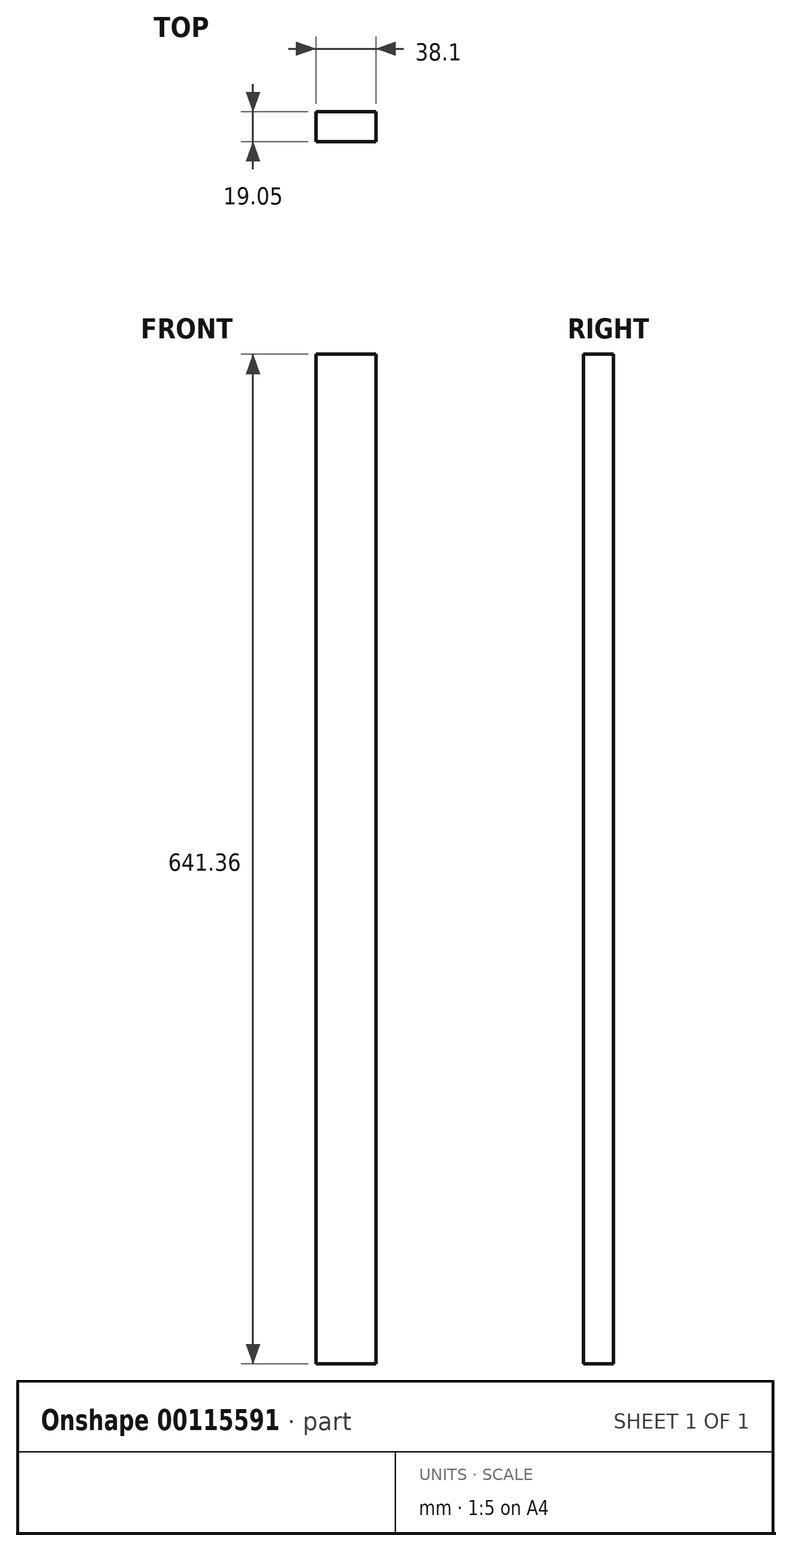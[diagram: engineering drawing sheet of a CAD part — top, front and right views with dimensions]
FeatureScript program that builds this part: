
annotation { "Feature Type Name" : "Feature", "Feature Type Description" : "" }
export const myFeature = defineFeature(function(context is Context, id is Id, definition is map)
    precondition{}
    {
        {
            var Q0;
            Q0=qCreatedBy(makeId("Front.planeOp"),FACE);
            var sketch = newSketch(context, id + "F0", { "sketchPlane" : qUnion([Q0])});
            skLineSegment(sketch, "E0.bottom", {"start": v(-19.05, 320.68) * mm, "end": v(19.05, 320.68) * mm});
            skLineSegment(sketch, "E0.top", {"start": v(-19.05, -320.68) * mm, "end": v(19.05, -320.68) * mm});
            skLineSegment(sketch, "E0.left", {"start": v(-19.05, 320.68) * mm, "end": v(-19.05, -320.68) * mm});
            skLineSegment(sketch, "E0.right", {"start": v(19.05, 320.68) * mm, "end": v(19.05, -320.68) * mm});
            skPoint(sketch, "E0.middle", {"position": v(0, 0) * mm});
            skSolve(sketch);
        }
        {
            var Q0;
            Q0=makeQuery(id+"F0.imprint","IMPRINT",FACE,{"disambiguationData":[TD([[makeQuery(id+"F0.imprint","IMPRINT",EDGE,{"derivedFrom":sQuery(id+"F0.wireOp",EDGE,"E0.bottom")}),-1.0]])]});
            extrude(context, id + "F1", {"entities" : qUnion([Q0]), "depth" : 19.05 * mm});
        }
    });
